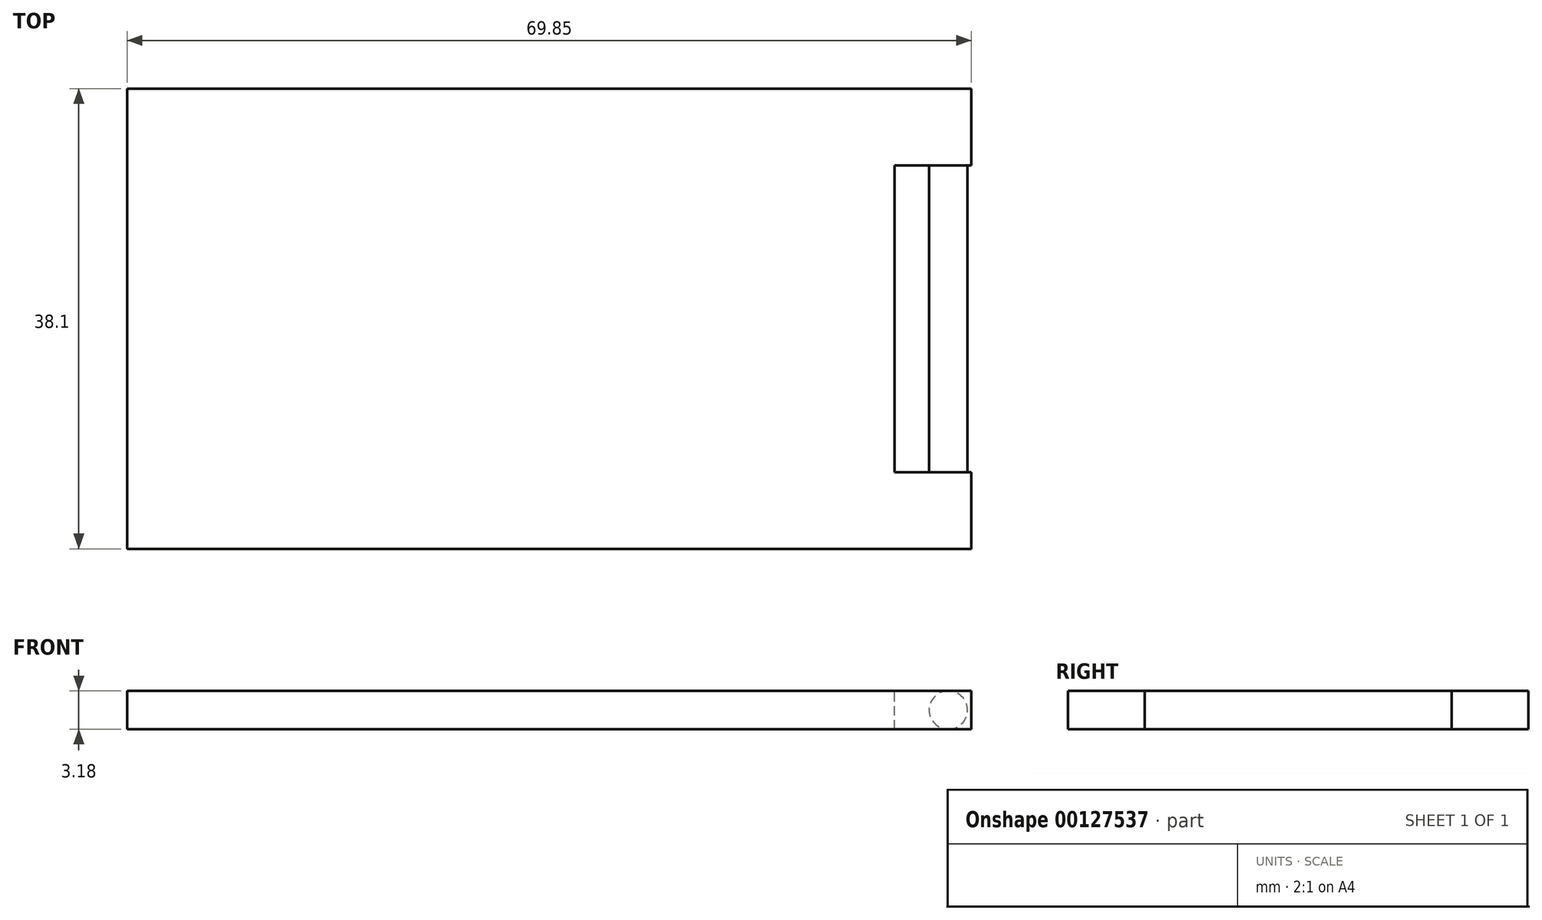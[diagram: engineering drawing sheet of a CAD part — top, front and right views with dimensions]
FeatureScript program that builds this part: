
annotation { "Feature Type Name" : "Feature", "Feature Type Description" : "" }
export const myFeature = defineFeature(function(context is Context, id is Id, definition is map)
    precondition{}
    {
        {
            var Q0;
            Q0=qCreatedBy(makeId("Top.planeOp"),FACE);
            var sketch = newSketch(context, id + "F0", { "sketchPlane" : qUnion([Q0])});
            skLineSegment(sketch, "E0.bottom", {"start": v(-6.45, 93.72) * mm, "end": v(57.05, 93.72) * mm});
            skLineSegment(sketch, "E0.top", {"start": v(-6.45, 55.62) * mm, "end": v(57.05, 55.62) * mm});
            skLineSegment(sketch, "E0.left", {"start": v(-6.45, 93.72) * mm, "end": v(-6.45, 55.62) * mm});
            skLineSegment(sketch, "E0.right", {"start": v(57.05, 93.72) * mm, "end": v(57.05, 55.62) * mm});
            skSolve(sketch);
        }
        {
            var Q0;
            Q0 = qSketchRegion(id + "F0", true);
            extrude(context, id + "F1", {"entities" : qUnion([Q0]), "depth" : 3.17 * mm});
        }
        {
            var Q0;
            Q0=makeQuery(id+"F1.opExtrude","SWEPT_FACE",FACE,{"disambiguationData":[OSD([sQuery(id+"F0.wireOp",EDGE,"E0.right")])]});
            var sketch = newSketch(context, id + "F2", { "sketchPlane" : qUnion([Q0])});
            skLineSegment(sketch, "E1.bottom", {"start": v(55.62, 0) * mm, "end": v(61.97, 0) * mm});
            skLineSegment(sketch, "E1.top", {"start": v(55.62, 3.18) * mm, "end": v(61.97, 3.18) * mm});
            skLineSegment(sketch, "E1.left", {"start": v(55.62, 0) * mm, "end": v(55.62, 3.18) * mm});
            skLineSegment(sketch, "E1.right", {"start": v(61.97, 0) * mm, "end": v(61.97, 3.18) * mm});
            skLineSegment(sketch, "E2.bottom", {"start": v(93.72, 0) * mm, "end": v(87.37, 0) * mm});
            skLineSegment(sketch, "E2.top", {"start": v(93.72, 3.18) * mm, "end": v(87.37, 3.18) * mm});
            skLineSegment(sketch, "E2.left", {"start": v(93.72, 0) * mm, "end": v(93.72, 3.18) * mm});
            skLineSegment(sketch, "E2.right", {"start": v(87.37, 0) * mm, "end": v(87.37, 3.18) * mm});
            skSolve(sketch);
        }
        {
            var Q0;
            Q0 = qSketchRegion(id + "F2", true);
            extrude(context, id + "F3", {"entities" : qUnion([Q0]), "operationType" : NewBodyOperationType.ADD, "depth" : 6.35 * mm});
        }
        {
            var Q0;
            Q0=makeQuery(id+"F3.opExtrude","SWEPT_FACE",FACE,{"disambiguationData":[OSD([sQuery(id+"F2.wireOp",EDGE,"E1.right")])]});
            var sketch = newSketch(context, id + "F4", { "sketchPlane" : qUnion([Q0])});
            skCircle(sketch, "E3", {"center": v(-61.5, 1.59) * mm, "radius": 1.59 * mm});
            skPoint(sketch, "E3.centerSnap0", {"position": v(-63.4, 1.59) * mm});
            skSolve(sketch);
        }
        {
            var Q0;
            Q0 = qSketchRegion(id + "F4", true);
            var Q1;
            Q1=makeQuery(id+"F3.opExtrude","SWEPT_FACE",FACE,{"disambiguationData":[OSD([sQuery(id+"F2.wireOp",EDGE,"E2.right")])]});
            extrude(context, id + "F5", {"entities" : qUnion([Q0]), "operationType" : NewBodyOperationType.ADD, "endBoundEntityFace" : qUnion([Q1]), "depth" : 25.4 * mm});
        }
    });
